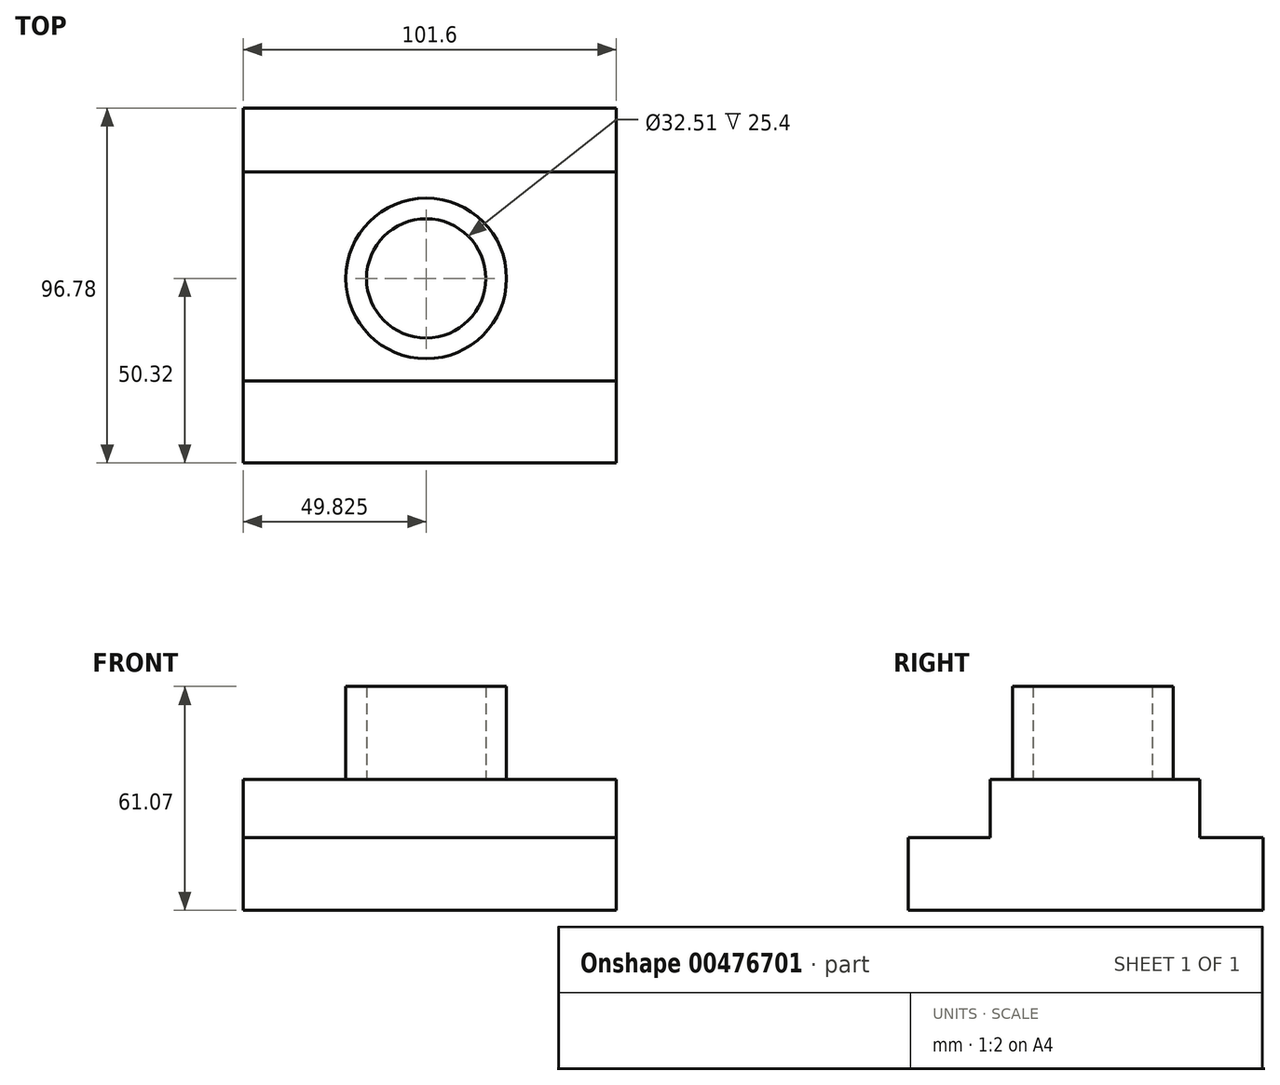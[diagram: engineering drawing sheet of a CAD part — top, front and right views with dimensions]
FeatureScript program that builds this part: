
annotation { "Feature Type Name" : "Feature", "Feature Type Description" : "" }
export const myFeature = defineFeature(function(context is Context, id is Id, definition is map)
    precondition{}
    {
        {
            var Q0;
            Q0=qCreatedBy(makeId("Right.planeOp"),FACE);
            var sketch = newSketch(context, id + "F0", { "sketchPlane" : qUnion([Q0])});
            skLineSegment(sketch, "E0", {"start": v(0, 0) * mm, "end": v(-50.32, 0) * mm});
            skLineSegment(sketch, "E1", {"start": v(0, 0) * mm, "end": v(46.46, 0) * mm});
            skLineSegment(sketch, "E2", {"start": v(-50.32, 0) * mm, "end": v(-50.32, 19.86) * mm});
            skLineSegment(sketch, "E3", {"start": v(-50.32, 19.86) * mm, "end": v(-27.96, 19.86) * mm});
            skLineSegment(sketch, "E4", {"start": v(-27.96, 19.86) * mm, "end": v(-27.96, 35.67) * mm});
            skLineSegment(sketch, "E5", {"start": v(-27.96, 35.67) * mm, "end": v(29.11, 35.67) * mm});
            skLineSegment(sketch, "E6", {"start": v(29.11, 35.67) * mm, "end": v(29.11, 19.86) * mm});
            skLineSegment(sketch, "E7", {"start": v(29.11, 19.86) * mm, "end": v(46.46, 19.86) * mm});
            skLineSegment(sketch, "E8", {"start": v(46.46, 19.86) * mm, "end": v(46.46, 0) * mm});
            skSolve(sketch);
        }
        {
            var Q0;
            Q0 = qSketchRegion(id + "F0", true);
            extrude(context, id + "F1", {"entities" : qUnion([Q0]), "depth" : 25.4 * mm});
        }
        {
            var Q0;
            Q0=makeQuery(id+"F1.opExtrude","CAP_FACE",FACE,{"disambiguationData":[OSD([sQuery(id+"F0.wireOp",EDGE,"E0"),sQuery(id+"F0.wireOp",EDGE,"E1"),sQuery(id+"F0.wireOp",EDGE,"E2"),sQuery(id+"F0.wireOp",EDGE,"E3"),sQuery(id+"F0.wireOp",EDGE,"E4"),sQuery(id+"F0.wireOp",EDGE,"E5"),sQuery(id+"F0.wireOp",EDGE,"E6"),sQuery(id+"F0.wireOp",EDGE,"E7"),sQuery(id+"F0.wireOp",EDGE,"E8")])],"isStart":false});
            extrude(context, id + "F2", {"entities" : qUnion([Q0]), "operationType" : NewBodyOperationType.ADD, "depth" : 25.4 * mm});
        }
        {
            var Q0;
            Q0=makeQuery(id+"F2.opExtrude","CAP_FACE",FACE,{"disambiguationData":[OSD([sQuery(id+"F0.wireOp",EDGE,"E0"),sQuery(id+"F0.wireOp",EDGE,"E1"),sQuery(id+"F0.wireOp",EDGE,"E2"),sQuery(id+"F0.wireOp",EDGE,"E3"),sQuery(id+"F0.wireOp",EDGE,"E4"),sQuery(id+"F0.wireOp",EDGE,"E5"),sQuery(id+"F0.wireOp",EDGE,"E6"),sQuery(id+"F0.wireOp",EDGE,"E7"),sQuery(id+"F0.wireOp",EDGE,"E8")])],"isStart":false});
            extrude(context, id + "F3", {"entities" : qUnion([Q0]), "operationType" : NewBodyOperationType.ADD, "depth" : 25.4 * mm});
        }
        {
            var Q0;
            Q0=makeQuery(id+"F3.opExtrude","CAP_FACE",FACE,{"disambiguationData":[OSD([sQuery(id+"F0.wireOp",EDGE,"E0"),sQuery(id+"F0.wireOp",EDGE,"E1"),sQuery(id+"F0.wireOp",EDGE,"E2"),sQuery(id+"F0.wireOp",EDGE,"E3"),sQuery(id+"F0.wireOp",EDGE,"E4"),sQuery(id+"F0.wireOp",EDGE,"E5"),sQuery(id+"F0.wireOp",EDGE,"E6"),sQuery(id+"F0.wireOp",EDGE,"E7"),sQuery(id+"F0.wireOp",EDGE,"E8")])],"isStart":false});
            extrude(context, id + "F4", {"entities" : qUnion([Q0]), "operationType" : NewBodyOperationType.ADD, "depth" : 25.4 * mm});
        }
        {
            var Q0;
            {var subQ0=sQuery(id+"F0.wireOp",EDGE,"E5");Q0=makeQuery(id+"F4.boolean.opBoolean","MERGE",FACE,{"derivedFrom":[makeQuery(id+"F3.boolean.opBoolean","MERGE",FACE,{"derivedFrom":[makeQuery(id+"F2.boolean.opBoolean","MERGE",FACE,{"derivedFrom":[makeQuery(id+"F1.opExtrude","SWEPT_FACE",FACE,{"disambiguationData":[OSD([subQ0])]}),makeQuery(id+"F2.opExtrude","SWEPT_FACE",FACE,{"disambiguationData":[OSD([subQ0])]})]}),makeQuery(id+"F3.opExtrude","SWEPT_FACE",FACE,{"disambiguationData":[OSD([subQ0])]})]}),makeQuery(id+"F4.opExtrude","SWEPT_FACE",FACE,{"disambiguationData":[OSD([subQ0])]})]});}
            var sketch = newSketch(context, id + "F5", { "sketchPlane" : qUnion([Q0])});
            skSolve(sketch);
        }
        {
            var Q0;
            {var subQ0=sQuery(id+"F0.wireOp",EDGE,"E5");Q0=makeQuery(id+"F5.imprint","IMPRINT",FACE,{"disambiguationData":[TD([[makeQuery(id+"F5.imprint","IMPRINT",EDGE,{"derivedFrom":makeQuery(id+"F1.opExtrude","CAP_EDGE",EDGE,{"disambiguationData":[OSD([subQ0])],"isStart":true})}),-1.0]])]});}
            var sketch = newSketch(context, id + "F6", { "sketchPlane" : qUnion([Q0])});
            skCircle(sketch, "E9", {"center": v(49.82, 0) * mm, "radius": 21.92 * mm});
            skCircle(sketch, "E10", {"center": v(49.82, 0) * mm, "radius": 16.25 * mm});
            skSolve(sketch);
        }
        {
            var Q0;
            Q0=makeQuery(id+"F6.imprint","IMPRINT",FACE,{"disambiguationData":[TD([[makeQuery(id+"F6.imprint","IMPRINT",EDGE,{"derivedFrom":sQuery(id+"F6.wireOp",EDGE,"E9")}),1.0]])]});
            extrude(context, id + "F7", {"entities" : qUnion([Q0]), "operationType" : NewBodyOperationType.ADD, "depth" : 25.4 * mm, "hasSecondDirection" : true, "secondDirectionOppositeDirection" : true, "secondDirectionDepth" : 25.4 * mm});
        }
    });
